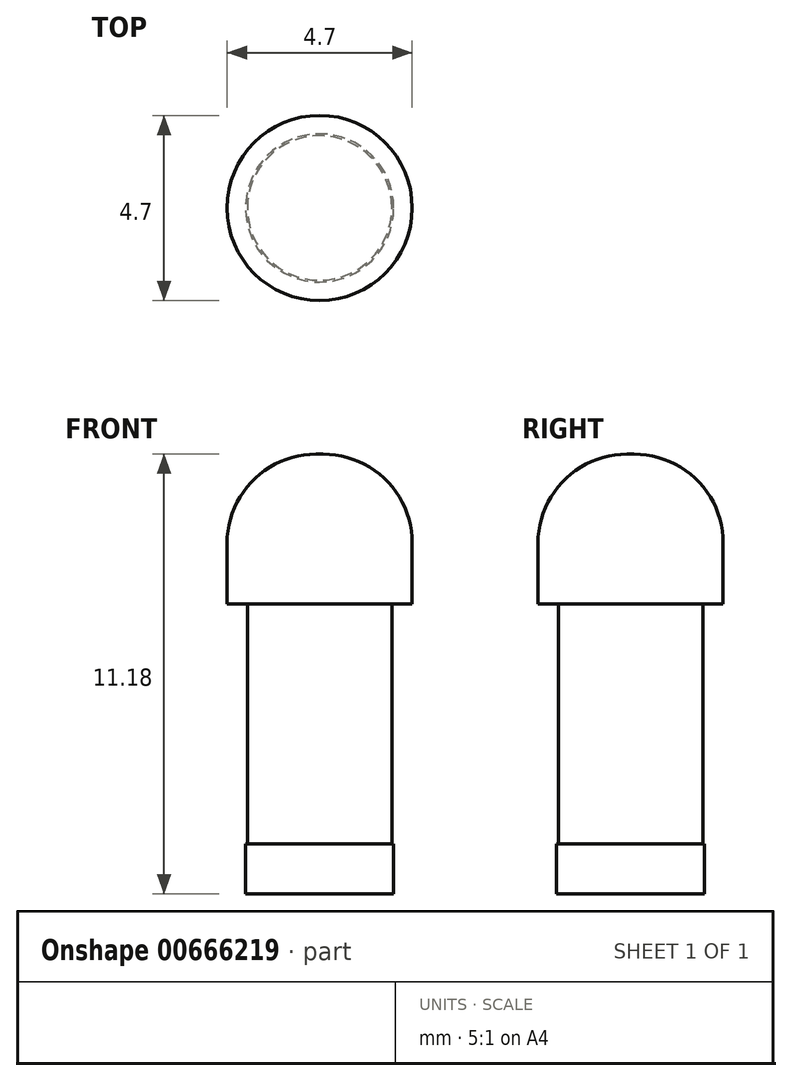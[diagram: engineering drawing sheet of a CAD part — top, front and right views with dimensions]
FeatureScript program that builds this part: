
annotation { "Feature Type Name" : "Feature", "Feature Type Description" : "" }
export const myFeature = defineFeature(function(context is Context, id is Id, definition is map)
    precondition{}
    {
        {
            var Q0;
            Q0=qCreatedBy(makeId("Top.planeOp"),FACE);
            var sketch = newSketch(context, id + "F0", { "sketchPlane" : qUnion([Q0])});
            skCircle(sketch, "E0", {"center": v(0, 0) * mm, "radius": 1.84 * mm});
            skSolve(sketch);
        }
        {
            var Q0;
            Q0=makeQuery(id+"F0.imprint","IMPRINT",FACE,{"disambiguationData":[TD([[makeQuery(id+"F0.imprint","IMPRINT",EDGE,{"derivedFrom":sQuery(id+"F0.wireOp",EDGE,"E0")}),1.0]])]});
            extrude(context, id + "F1", {"entities" : qUnion([Q0]), "depth" : 6.1 * mm, "offsetDistance" : 25.4 * mm});
        }
        {
            var Q0;
            Q0=makeQuery(id+"F1.opExtrude","CAP_FACE",FACE,{"disambiguationData":[OSD([sQuery(id+"F0.wireOp",EDGE,"E0")])],"isStart":false});
            var sketch = newSketch(context, id + "F2", { "sketchPlane" : qUnion([Q0])});
            skCircle(sketch, "E1", {"center": v(0, 0) * mm, "radius": 2.35 * mm});
            skSolve(sketch);
        }
        {
            var Q0;
            Q0=makeQuery(id+"F2.imprint","IMPRINT",FACE,{"disambiguationData":[TD([[makeQuery(id+"F2.imprint","IMPRINT",EDGE,{"derivedFrom":sQuery(id+"F2.wireOp",EDGE,"E1")}),1.0]])]});
            var Q1;
            Q1=makeQuery(id+"F2.imprint","IMPRINT",FACE,{"disambiguationData":[TD([[makeQuery(id+"F2.imprint","IMPRINT",EDGE,{"derivedFrom":makeQuery(id+"F1.opExtrude","CAP_EDGE",EDGE,{"disambiguationData":[OSD([sQuery(id+"F0.wireOp",EDGE,"E0")])],"isStart":false})}),1.0]])]});
            extrude(context, id + "F3", {"entities" : qUnion([Q0, Q1]), "depth" : 3.8 * mm, "offsetDistance" : 25.4 * mm});
        }
        {
            var Q0;
            Q0=makeQuery(id+"F3.opExtrude","CAP_FACE",FACE,{"disambiguationData":[OSD([sQuery(id+"F2.wireOp",EDGE,"E1")])],"isStart":false});
            fillet(context, id + "F4", {"entities" : qUnion([Q0]), "radius" : 2.26 * mm, "tangentPropagation" : true, "allowEdgeOverflow" : false});
        }
        {
            var Q0;
            Q0=makeQuery(id+"F1.opExtrude","CAP_FACE",FACE,{"disambiguationData":[OSD([sQuery(id+"F0.wireOp",EDGE,"E0")])],"isStart":true});
            var sketch = newSketch(context, id + "F5", { "sketchPlane" : qUnion([Q0])});
            skCircle(sketch, "E2", {"center": v(0, 0) * mm, "radius": 1.88 * mm});
            skSolve(sketch);
        }
        {
            var Q0;
            Q0=makeQuery(id+"F5.imprint","IMPRINT",FACE,{"disambiguationData":[TD([[makeQuery(id+"F5.imprint","IMPRINT",EDGE,{"derivedFrom":sQuery(id+"F5.wireOp",EDGE,"E2")}),1.0]])]});
            var Q1;
            Q1=makeQuery(id+"F5.imprint","IMPRINT",FACE,{"disambiguationData":[TD([[makeQuery(id+"F5.imprint","IMPRINT",EDGE,{"derivedFrom":makeQuery(id+"F1.opExtrude","CAP_EDGE",EDGE,{"disambiguationData":[OSD([sQuery(id+"F0.wireOp",EDGE,"E0")])],"isStart":true})}),-1.0]])]});
            extrude(context, id + "F6", {"entities" : qUnion([Q0, Q1]), "depth" : 1.27 * mm, "offsetDistance" : 25.4 * mm});
        }
    });
